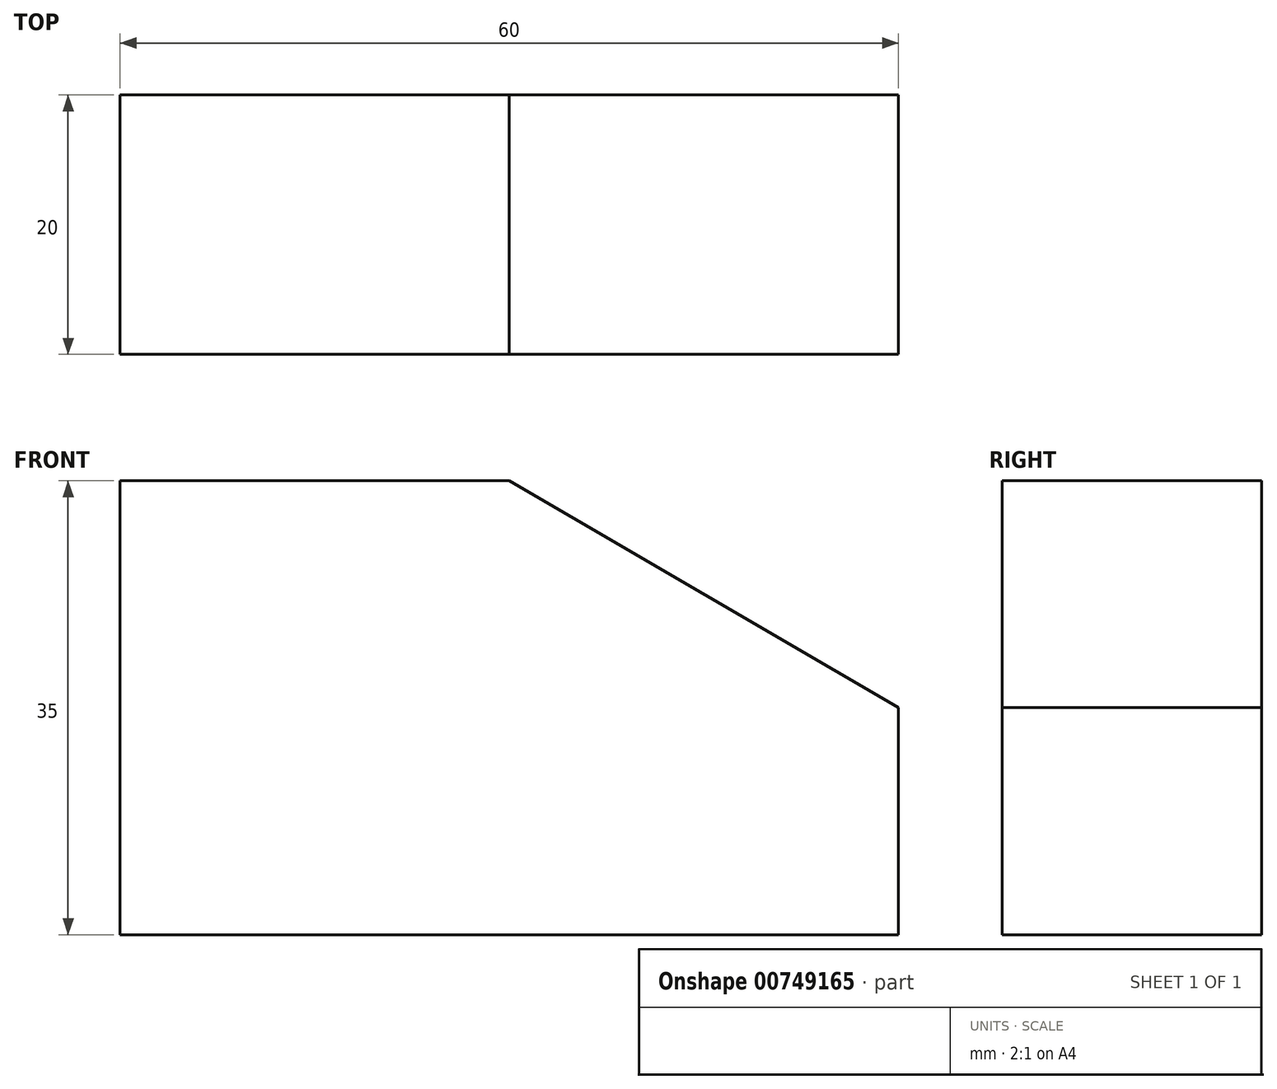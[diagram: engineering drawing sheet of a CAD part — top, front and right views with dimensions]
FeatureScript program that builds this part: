
annotation { "Feature Type Name" : "Feature", "Feature Type Description" : "" }
export const myFeature = defineFeature(function(context is Context, id is Id, definition is map)
    precondition{}
    {
        {
            var Q0;
            Q0=qCreatedBy(makeId("Front.planeOp"),FACE);
            var sketch = newSketch(context, id + "F0", { "sketchPlane" : qUnion([Q0])});
            skLineSegment(sketch, "E0", {"start": v(0, 0) * mm, "end": v(0, 35) * mm});
            skLineSegment(sketch, "E1", {"start": v(0, 35) * mm, "end": v(30, 35) * mm});
            skLineSegment(sketch, "E2", {"start": v(30, 35) * mm, "end": v(60, 17.5) * mm});
            skLineSegment(sketch, "E3", {"start": v(60, 17.5) * mm, "end": v(60, 0) * mm});
            skLineSegment(sketch, "E4", {"start": v(60, 0) * mm, "end": v(0, 0) * mm});
            skSolve(sketch);
        }
        {
            var Q0;
            Q0=makeQuery(id+"F0.imprint","IMPRINT",FACE,{"disambiguationData":[TD([[makeQuery(id+"F0.imprint","IMPRINT",EDGE,{"derivedFrom":sQuery(id+"F0.wireOp",EDGE,"E0")}),-1.0]])]});
            extrude(context, id + "F1", {"entities" : qUnion([Q0]), "depth" : 20 * mm, "offsetDistance" : 25 * mm});
        }
    });
